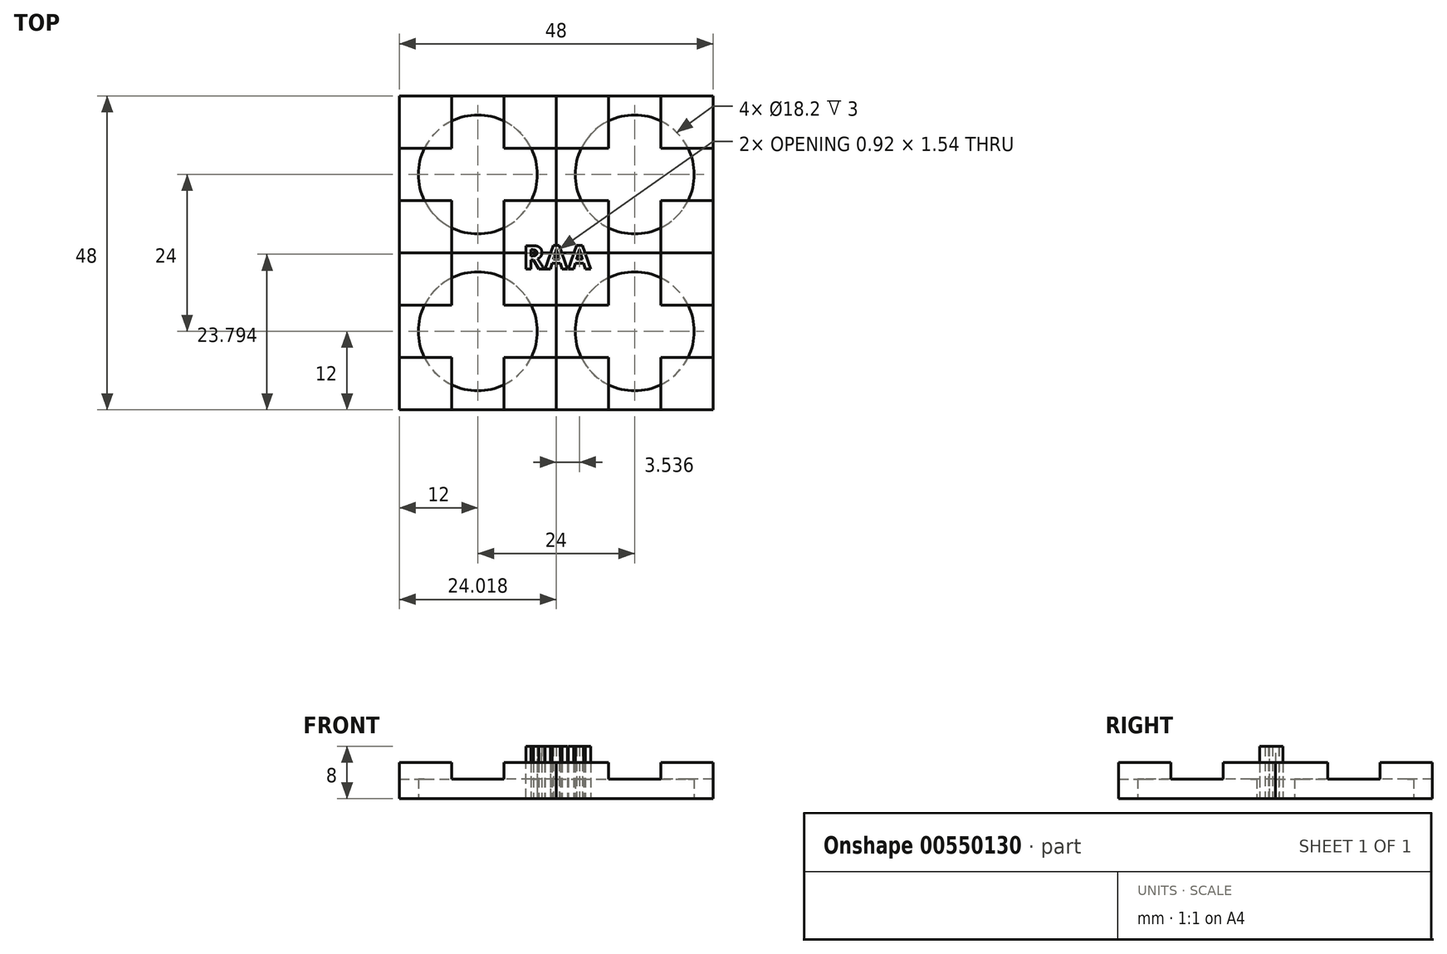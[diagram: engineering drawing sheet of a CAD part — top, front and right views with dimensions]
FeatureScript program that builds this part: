
annotation { "Feature Type Name" : "Feature", "Feature Type Description" : "" }
export const myFeature = defineFeature(function(context is Context, id is Id, definition is map)
    precondition{}
    {
        {
            var Q0;
            Q0=qCreatedBy(makeId("Top.planeOp"),FACE);
            var sketch = newSketch(context, id + "F0", { "sketchPlane" : qUnion([Q0])});
            skLineSegment(sketch, "E0.bottom", {"start": v(12, -12) * mm, "end": v(-12, -12) * mm});
            skLineSegment(sketch, "E0.top", {"start": v(12, 12) * mm, "end": v(-12, 12) * mm});
            skLineSegment(sketch, "E0.left", {"start": v(12, -12) * mm, "end": v(12, 12) * mm});
            skLineSegment(sketch, "E0.right", {"start": v(-12, -12) * mm, "end": v(-12, 12) * mm});
            skPoint(sketch, "E0.middle", {"position": v(0, 0) * mm});
            skCircle(sketch, "E1", {"center": v(0, 0) * mm, "radius": 9.1 * mm});
            skSolve(sketch);
        }
        {
            var Q0;
            Q0=makeQuery(id+"F0.imprint","IMPRINT",FACE,{"disambiguationData":[TD([[makeQuery(id+"F0.imprint","IMPRINT",EDGE,{"derivedFrom":sQuery(id+"F0.wireOp",EDGE,"E0.bottom")}),-1.0]])]});
            extrude(context, id + "F1", {"entities" : qUnion([Q0]), "depth" : 3 * mm, "offsetDistance" : 25 * mm});
        }
        {
            var Q0;
            Q0=qCreatedBy(makeId("Top.planeOp"),FACE);
            var sketch = newSketch(context, id + "F2", { "sketchPlane" : qUnion([Q0])});
            skLineSegment(sketch, "E2", {"start": v(0, 0) * mm, "end": v(-12, 0) * mm});
            skLineSegment(sketch, "E3", {"start": v(-12, 0) * mm, "end": v(-12, 12) * mm});
            skLineSegment(sketch, "E4.bottom", {"start": v(-12, 12) * mm, "end": v(-4, 12) * mm});
            skLineSegment(sketch, "E4.top", {"start": v(-12, 4) * mm, "end": v(-4, 4) * mm});
            skLineSegment(sketch, "E4.left", {"start": v(-12, 12) * mm, "end": v(-12, 4) * mm});
            skLineSegment(sketch, "E4.right", {"start": v(-4, 12) * mm, "end": v(-4, 4) * mm});
            skSolve(sketch);
        }
        {
            var Q0;
            Q0 = qSketchRegion(id + "F2", true);
            extrude(context, id + "F3", {"entities" : qUnion([Q0]), "depth" : 2.5 * mm, "offsetDistance" : 25 * mm});
        }
        {
            var Q0;
            Q0=qCreatedBy(makeId("Front.planeOp"),FACE);
            var sketch = newSketch(context, id + "F4", { "sketchPlane" : qUnion([Q0])});
            skLineSegment(sketch, "E5", {"start": v(0, 0) * mm, "end": v(0, 12.34) * mm});
            skSolve(sketch);
        }
        {
            var Q0;
            Q0=makeQuery(id+"F3.opExtrude","SWEPT_BODY",BODY,{"disambiguationData":[OSD([sQuery(id+"F2.wireOp",EDGE,"E4.bottom"),sQuery(id+"F2.wireOp",EDGE,"E4.top"),sQuery(id+"F2.wireOp",EDGE,"E4.left"),sQuery(id+"F2.wireOp",EDGE,"E4.right")])]});
            transform(context, id + "F5", {"entities" : qUnion([Q0]), "transformType" : TransformType.TRANSLATION_3D, "dx" : 0 * mm, "dy" : 0 * mm, "dz" : 3 * mm, "makeCopy" : false});
        }
        {
            var Q0;
            Q0=makeQuery(id+"F3.opExtrude","SWEPT_BODY",BODY,{"disambiguationData":[OSD([sQuery(id+"F2.wireOp",EDGE,"E4.bottom"),sQuery(id+"F2.wireOp",EDGE,"E4.top"),sQuery(id+"F2.wireOp",EDGE,"E4.left"),sQuery(id+"F2.wireOp",EDGE,"E4.right")])]});
            var Q1;
            Q1=sQuery(id+"F4.wireOp",EDGE,"E5");
            circularPattern(context, id + "F6", {"entities" : qUnion([Q0]), "axis" : qUnion([Q1]), "angle" : 360 * degree, "instanceCount" : 4, "equalSpace" : true});
        }
        {
            var Q0;
            Q0=makeQuery(id+"F6.opPattern","COPY",BODY,{"derivedFrom":makeQuery(id+"F3.opExtrude","SWEPT_BODY",BODY,{"disambiguationData":[OSD([sQuery(id+"F2.wireOp",EDGE,"E4.bottom"),sQuery(id+"F2.wireOp",EDGE,"E4.top"),sQuery(id+"F2.wireOp",EDGE,"E4.left"),sQuery(id+"F2.wireOp",EDGE,"E4.right")])]}),"instanceName":"3"});
            var Q1;
            Q1=makeQuery(id+"F3.opExtrude","SWEPT_BODY",BODY,{"disambiguationData":[OSD([sQuery(id+"F2.wireOp",EDGE,"E4.bottom"),sQuery(id+"F2.wireOp",EDGE,"E4.top"),sQuery(id+"F2.wireOp",EDGE,"E4.left"),sQuery(id+"F2.wireOp",EDGE,"E4.right")])]});
            var Q2;
            Q2=makeQuery(id+"F6.opPattern","COPY",BODY,{"derivedFrom":makeQuery(id+"F3.opExtrude","SWEPT_BODY",BODY,{"disambiguationData":[OSD([sQuery(id+"F2.wireOp",EDGE,"E4.bottom"),sQuery(id+"F2.wireOp",EDGE,"E4.top"),sQuery(id+"F2.wireOp",EDGE,"E4.left"),sQuery(id+"F2.wireOp",EDGE,"E4.right")])]}),"instanceName":"2"});
            var Q3;
            Q3=makeQuery(id+"F1.opExtrude","SWEPT_BODY",BODY,{"disambiguationData":[OSD([sQuery(id+"F0.wireOp",EDGE,"E0.bottom"),sQuery(id+"F0.wireOp",EDGE,"E0.top"),sQuery(id+"F0.wireOp",EDGE,"E0.left"),sQuery(id+"F0.wireOp",EDGE,"E0.right"),sQuery(id+"F0.wireOp",EDGE,"E1")])]});
            var Q4;
            Q4=makeQuery(id+"F6.opPattern","COPY",BODY,{"derivedFrom":makeQuery(id+"F3.opExtrude","SWEPT_BODY",BODY,{"disambiguationData":[OSD([sQuery(id+"F2.wireOp",EDGE,"E4.bottom"),sQuery(id+"F2.wireOp",EDGE,"E4.top"),sQuery(id+"F2.wireOp",EDGE,"E4.left"),sQuery(id+"F2.wireOp",EDGE,"E4.right")])]}),"instanceName":"1"});
            booleanBodies(context, id + "F7", {"operationType" : BooleanOperationType.UNION, "tools" : qUnion([Q0, Q1, Q2, Q3, Q4])});
        }
        {
            var Q0;
            Q0=makeQuery(id+"F6.opPattern","COPY",BODY,{"derivedFrom":makeQuery(id+"F3.opExtrude","SWEPT_BODY",BODY,{"disambiguationData":[OSD([sQuery(id+"F2.wireOp",EDGE,"E4.bottom"),sQuery(id+"F2.wireOp",EDGE,"E4.top"),sQuery(id+"F2.wireOp",EDGE,"E4.left"),sQuery(id+"F2.wireOp",EDGE,"E4.right")])]}),"instanceName":"3"});
            var Q1;
            Q1=makeQuery(id+"F7.opBoolean","MERGE",EDGE,{"derivedFrom":[makeQuery(id+"F1.opExtrude","SWEPT_EDGE",EDGE,{"disambiguationData":[OSD([sQuery(id+"F0.wireOp",EDGE,"E0.bottom"),sQuery(id+"F0.wireOp",EDGE,"E0.left")])]}),makeQuery(id+"F6.opPattern","COPY",EDGE,{"derivedFrom":makeQuery(id+"F3.opExtrude","SWEPT_EDGE",EDGE,{"disambiguationData":[OSD([sQuery(id+"F2.wireOp",EDGE,"E4.bottom"),sQuery(id+"F2.wireOp",EDGE,"E4.left")])]}),"instanceName":"2"})]});
            circularPattern(context, id + "F8", {"entities" : qUnion([Q0]), "axis" : qUnion([Q1]), "angle" : 360 * degree, "instanceCount" : 4, "equalSpace" : true});
        }
        {
            var Q0;
            Q0=qCreatedBy(makeId("Top.planeOp"),FACE);
            var sketch = newSketch(context, id + "F9", { "sketchPlane" : qUnion([Q0])});
            skText(sketch, "E6", { "text": "RAA", "fontName": "OpenSans-Bold.ttf"});
            const initialGuessF9  = {"E6": [0.00466, -0.01745, 1, 0, 0.00358]};
            skSetInitialGuess(sketch, initialGuessF9);
            skSolve(sketch);
        }
        {
            var Q0;
            Q0 = qSketchRegion(id + "F9", true);
            extrude(context, id + "F10", {"entities" : qUnion([Q0]), "depth" : 8 * mm, "offsetDistance" : 25 * mm});
        }
        {
            var Q0;
            Q0=makeQuery(id+"F10.opExtrude","SWEPT_BODY",BODY,{"disambiguationData":[OSD([sQuery(id+"F9.wireOp",EDGE,"E6.sketch_text.stroke-0"),sQuery(id+"F9.wireOp",EDGE,"E6.sketch_text.stroke-1"),sQuery(id+"F9.wireOp",EDGE,"E6.sketch_text.stroke-2"),sQuery(id+"F9.wireOp",EDGE,"E6.sketch_text.stroke-3"),sQuery(id+"F9.wireOp",EDGE,"E6.sketch_text.stroke-4"),sQuery(id+"F9.wireOp",EDGE,"E6.sketch_text.stroke-5"),sQuery(id+"F9.wireOp",EDGE,"E6.sketch_text.stroke-6"),sQuery(id+"F9.wireOp",EDGE,"E6.sketch_text.stroke-7"),sQuery(id+"F9.wireOp",EDGE,"E6.sketch_text.stroke-8"),sQuery(id+"F9.wireOp",EDGE,"E6.sketch_text.stroke-9"),sQuery(id+"F9.wireOp",EDGE,"E6.sketch_text.stroke-10"),sQuery(id+"F9.wireOp",EDGE,"E6.sketch_text.stroke-11"),sQuery(id+"F9.wireOp",EDGE,"E6.sketch_text.stroke-12"),sQuery(id+"F9.wireOp",EDGE,"E6.sketch_text.stroke-13"),sQuery(id+"F9.wireOp",EDGE,"E6.sketch_text.stroke-14"),sQuery(id+"F9.wireOp",EDGE,"E6.sketch_text.stroke-15"),sQuery(id+"F9.wireOp",EDGE,"E6.sketch_text.stroke-16"),sQuery(id+"F9.wireOp",EDGE,"E6.sketch_text.stroke-17"),sQuery(id+"F9.wireOp",EDGE,"E6.sketch_text.stroke-18")])]});
            var Q1;
            Q1=makeQuery(id+"F10.opExtrude","SWEPT_BODY",BODY,{"disambiguationData":[OSD([sQuery(id+"F9.wireOp",EDGE,"E6.sketch_text.stroke-19"),sQuery(id+"F9.wireOp",EDGE,"E6.sketch_text.stroke-20"),sQuery(id+"F9.wireOp",EDGE,"E6.sketch_text.stroke-21"),sQuery(id+"F9.wireOp",EDGE,"E6.sketch_text.stroke-22"),sQuery(id+"F9.wireOp",EDGE,"E6.sketch_text.stroke-23"),sQuery(id+"F9.wireOp",EDGE,"E6.sketch_text.stroke-24"),sQuery(id+"F9.wireOp",EDGE,"E6.sketch_text.stroke-25"),sQuery(id+"F9.wireOp",EDGE,"E6.sketch_text.stroke-26"),sQuery(id+"F9.wireOp",EDGE,"E6.sketch_text.stroke-27"),sQuery(id+"F9.wireOp",EDGE,"E6.sketch_text.stroke-28"),sQuery(id+"F9.wireOp",EDGE,"E6.sketch_text.stroke-29"),sQuery(id+"F9.wireOp",EDGE,"E6.sketch_text.stroke-30")])]});
            var Q2;
            Q2=makeQuery(id+"F10.opExtrude","SWEPT_BODY",BODY,{"disambiguationData":[OSD([sQuery(id+"F9.wireOp",EDGE,"E6.sketch_text.stroke-31"),sQuery(id+"F9.wireOp",EDGE,"E6.sketch_text.stroke-32"),sQuery(id+"F9.wireOp",EDGE,"E6.sketch_text.stroke-33"),sQuery(id+"F9.wireOp",EDGE,"E6.sketch_text.stroke-34"),sQuery(id+"F9.wireOp",EDGE,"E6.sketch_text.stroke-35"),sQuery(id+"F9.wireOp",EDGE,"E6.sketch_text.stroke-36"),sQuery(id+"F9.wireOp",EDGE,"E6.sketch_text.stroke-37"),sQuery(id+"F9.wireOp",EDGE,"E6.sketch_text.stroke-38"),sQuery(id+"F9.wireOp",EDGE,"E6.sketch_text.stroke-39"),sQuery(id+"F9.wireOp",EDGE,"E6.sketch_text.stroke-40"),sQuery(id+"F9.wireOp",EDGE,"E6.sketch_text.stroke-41"),sQuery(id+"F9.wireOp",EDGE,"E6.sketch_text.stroke-42")])]});
            transform(context, id + "F11", {"entities" : qUnion([Q0, Q1, Q2]), "transformType" : TransformType.TRANSLATION_3D, "dx" : 2.25 * mm, "dy" : 3 * mm, "dz" : 0 * mm, "makeCopy" : false});
        }
        {
            var Q0;
            Q0=makeQuery(id+"F10.opExtrude","SWEPT_BODY",BODY,{"disambiguationData":[OSD([sQuery(id+"F9.wireOp",EDGE,"E6.sketch_text.stroke-0"),sQuery(id+"F9.wireOp",EDGE,"E6.sketch_text.stroke-1"),sQuery(id+"F9.wireOp",EDGE,"E6.sketch_text.stroke-2"),sQuery(id+"F9.wireOp",EDGE,"E6.sketch_text.stroke-3"),sQuery(id+"F9.wireOp",EDGE,"E6.sketch_text.stroke-4"),sQuery(id+"F9.wireOp",EDGE,"E6.sketch_text.stroke-5"),sQuery(id+"F9.wireOp",EDGE,"E6.sketch_text.stroke-6"),sQuery(id+"F9.wireOp",EDGE,"E6.sketch_text.stroke-7"),sQuery(id+"F9.wireOp",EDGE,"E6.sketch_text.stroke-8"),sQuery(id+"F9.wireOp",EDGE,"E6.sketch_text.stroke-9"),sQuery(id+"F9.wireOp",EDGE,"E6.sketch_text.stroke-10"),sQuery(id+"F9.wireOp",EDGE,"E6.sketch_text.stroke-11"),sQuery(id+"F9.wireOp",EDGE,"E6.sketch_text.stroke-12"),sQuery(id+"F9.wireOp",EDGE,"E6.sketch_text.stroke-13"),sQuery(id+"F9.wireOp",EDGE,"E6.sketch_text.stroke-14"),sQuery(id+"F9.wireOp",EDGE,"E6.sketch_text.stroke-15"),sQuery(id+"F9.wireOp",EDGE,"E6.sketch_text.stroke-16"),sQuery(id+"F9.wireOp",EDGE,"E6.sketch_text.stroke-17"),sQuery(id+"F9.wireOp",EDGE,"E6.sketch_text.stroke-18")])]});
            var Q1;
            Q1=makeQuery(id+"F10.opExtrude","SWEPT_BODY",BODY,{"disambiguationData":[OSD([sQuery(id+"F9.wireOp",EDGE,"E6.sketch_text.stroke-19"),sQuery(id+"F9.wireOp",EDGE,"E6.sketch_text.stroke-20"),sQuery(id+"F9.wireOp",EDGE,"E6.sketch_text.stroke-21"),sQuery(id+"F9.wireOp",EDGE,"E6.sketch_text.stroke-22"),sQuery(id+"F9.wireOp",EDGE,"E6.sketch_text.stroke-23"),sQuery(id+"F9.wireOp",EDGE,"E6.sketch_text.stroke-24"),sQuery(id+"F9.wireOp",EDGE,"E6.sketch_text.stroke-25"),sQuery(id+"F9.wireOp",EDGE,"E6.sketch_text.stroke-26"),sQuery(id+"F9.wireOp",EDGE,"E6.sketch_text.stroke-27"),sQuery(id+"F9.wireOp",EDGE,"E6.sketch_text.stroke-28"),sQuery(id+"F9.wireOp",EDGE,"E6.sketch_text.stroke-29"),sQuery(id+"F9.wireOp",EDGE,"E6.sketch_text.stroke-30")])]});
            var Q2;
            Q2=makeQuery(id+"F10.opExtrude","SWEPT_BODY",BODY,{"disambiguationData":[OSD([sQuery(id+"F9.wireOp",EDGE,"E6.sketch_text.stroke-31"),sQuery(id+"F9.wireOp",EDGE,"E6.sketch_text.stroke-32"),sQuery(id+"F9.wireOp",EDGE,"E6.sketch_text.stroke-33"),sQuery(id+"F9.wireOp",EDGE,"E6.sketch_text.stroke-34"),sQuery(id+"F9.wireOp",EDGE,"E6.sketch_text.stroke-35"),sQuery(id+"F9.wireOp",EDGE,"E6.sketch_text.stroke-36"),sQuery(id+"F9.wireOp",EDGE,"E6.sketch_text.stroke-37"),sQuery(id+"F9.wireOp",EDGE,"E6.sketch_text.stroke-38"),sQuery(id+"F9.wireOp",EDGE,"E6.sketch_text.stroke-39"),sQuery(id+"F9.wireOp",EDGE,"E6.sketch_text.stroke-40"),sQuery(id+"F9.wireOp",EDGE,"E6.sketch_text.stroke-41"),sQuery(id+"F9.wireOp",EDGE,"E6.sketch_text.stroke-42")])]});
            var Q3;
            Q3=makeQuery(id+"F6.opPattern","COPY",BODY,{"derivedFrom":makeQuery(id+"F3.opExtrude","SWEPT_BODY",BODY,{"disambiguationData":[OSD([sQuery(id+"F2.wireOp",EDGE,"E4.bottom"),sQuery(id+"F2.wireOp",EDGE,"E4.top"),sQuery(id+"F2.wireOp",EDGE,"E4.left"),sQuery(id+"F2.wireOp",EDGE,"E4.right")])]}),"instanceName":"3"});
            booleanBodies(context, id + "F12", {"operationType" : BooleanOperationType.UNION, "tools" : qUnion([Q0, Q1, Q2, Q3])});
        }
    });
